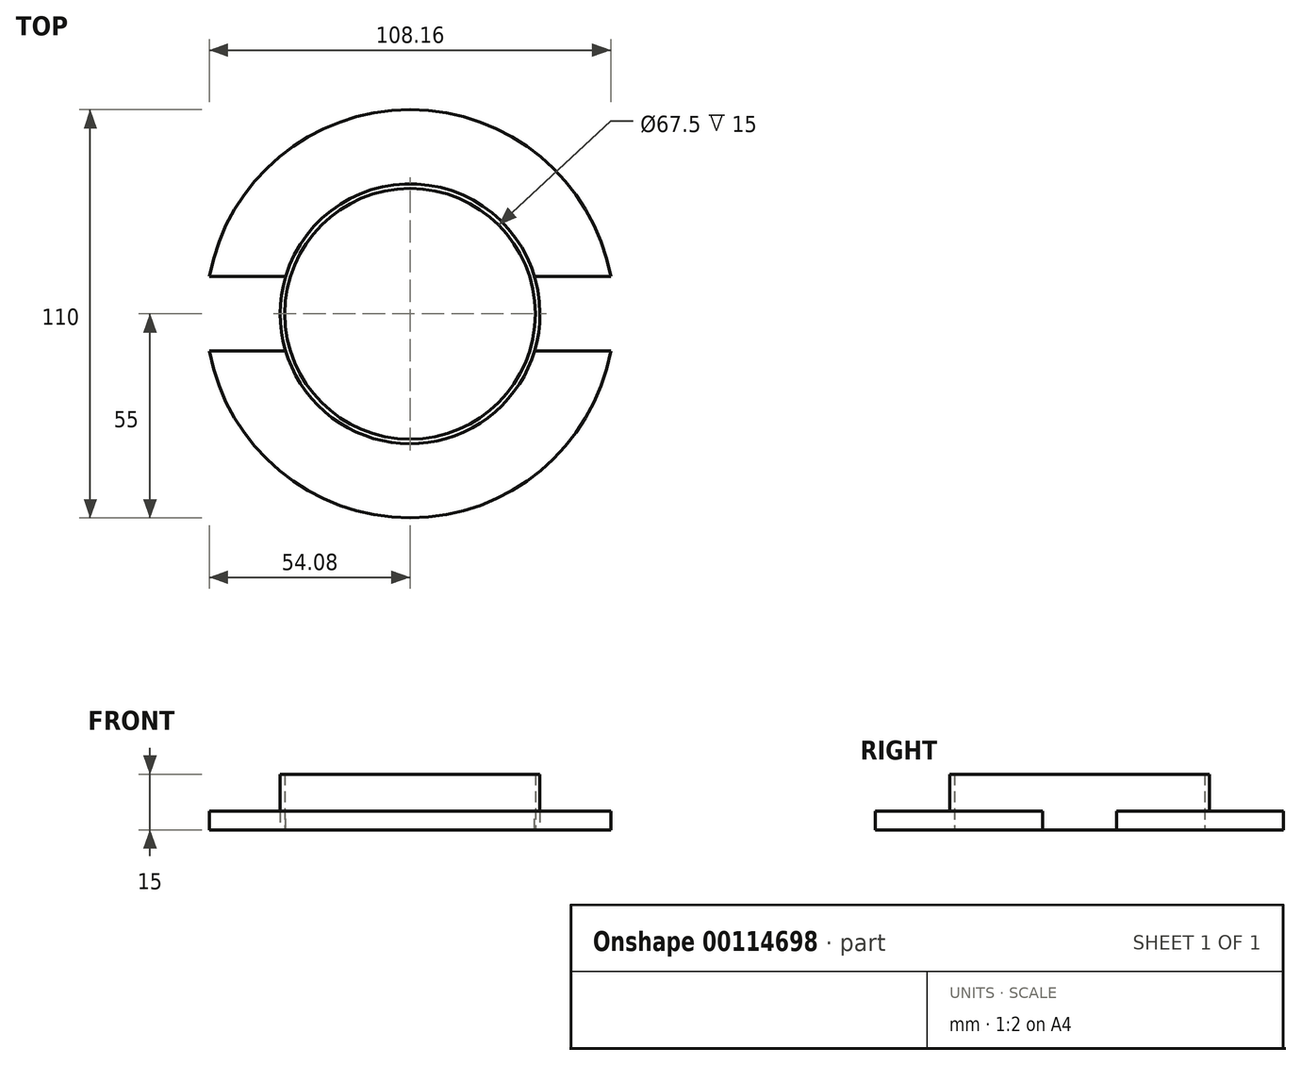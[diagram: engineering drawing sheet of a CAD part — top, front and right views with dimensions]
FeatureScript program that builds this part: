
annotation { "Feature Type Name" : "Feature", "Feature Type Description" : "" }
export const myFeature = defineFeature(function(context is Context, id is Id, definition is map)
    precondition{}
    {
        {
            var Q0;
            Q0=qCreatedBy(makeId("Top.planeOp"),FACE);
            var sketch = newSketch(context, id + "F0", { "sketchPlane" : qUnion([Q0])});
            skCircle(sketch, "E0", {"center": v(0, 0) * mm, "radius": 55 * mm});
            skCircle(sketch, "E1", {"center": v(0, 0) * mm, "radius": 33.75 * mm});
            skSolve(sketch);
        }
        {
            var Q0;
            Q0=makeQuery(id+"F0.imprint","IMPRINT",FACE,{"disambiguationData":[TD([[makeQuery(id+"F0.imprint","IMPRINT",EDGE,{"derivedFrom":sQuery(id+"F0.wireOp",EDGE,"E0")}),1.0]])]});
            extrude(context, id + "F1", {"entities" : qUnion([Q0]), "depth" : 5 * mm});
        }
        {
            var Q0;
            Q0=makeQuery(id+"F1.opExtrude","CAP_FACE",FACE,{"disambiguationData":[OSD([sQuery(id+"F0.wireOp",EDGE,"E0"),sQuery(id+"F0.wireOp",EDGE,"E1")])],"isStart":false});
            var sketch = newSketch(context, id + "F2", { "sketchPlane" : qUnion([Q0])});
            skCircle(sketch, "E2", {"center": v(0, 0) * mm, "radius": 35 * mm});
            skSolve(sketch);
        }
        {
            var Q0;
            Q0=makeQuery(id+"F2.imprint","IMPRINT",FACE,{"disambiguationData":[TD([[makeQuery(id+"F2.imprint","IMPRINT",EDGE,{"derivedFrom":sQuery(id+"F2.wireOp",EDGE,"E2")}),1.0]])]});
            extrude(context, id + "F3", {"entities" : qUnion([Q0]), "operationType" : NewBodyOperationType.ADD, "depth" : 10 * mm});
        }
        {
            var Q0;
            Q0=makeQuery(id+"F1.opExtrude","CAP_FACE",FACE,{"disambiguationData":[OSD([sQuery(id+"F0.wireOp",EDGE,"E0"),sQuery(id+"F0.wireOp",EDGE,"E1")])],"isStart":false});
            var sketch = newSketch(context, id + "F4", { "sketchPlane" : qUnion([Q0])});
            skLineSegment(sketch, "E3", {"start": v(0, 0) * mm, "end": v(0, 10) * mm});
            skLineSegment(sketch, "E4", {"start": v(0, 10) * mm, "end": v(33.54, 10) * mm});
            skLineSegment(sketch, "E5", {"start": v(33.54, 10) * mm, "end": v(61.18, 10) * mm});
            skLineSegment(sketch, "E6", {"start": v(61.18, 10) * mm, "end": v(61.18, -10) * mm});
            skLineSegment(sketch, "E7", {"start": v(61.18, -10) * mm, "end": v(33.54, -10) * mm});
            skLineSegment(sketch, "E8", {"start": v(-33.54, 10) * mm, "end": v(-64.6, 10) * mm});
            skLineSegment(sketch, "E9", {"start": v(-64.6, 10) * mm, "end": v(-64.6, -10) * mm});
            skLineSegment(sketch, "E10", {"start": v(-64.6, -10) * mm, "end": v(-33.54, -10) * mm});
            skCircle(sketch, "E11.0", {"center": v(0, 0) * mm, "radius": 35 * mm});
            skSolve(sketch);
        }
        {
            var Q0;
            {var subQ0=sQuery(id+"F4.wireOp",EDGE,"E11.0");var subQ1=sQuery(id+"F4.wireOp",EDGE,"E8");var subQ2=makeQuery(id+"F4.imprint","INTERSECT",VERTEX,{"derivedFrom":[subQ1,subQ0]});Q0=makeQuery(id+"F4.imprint","IMPRINT",FACE,{"disambiguationData":[TD([[makeQuery(id+"F4.imprint","IMPRINT",EDGE,{"disambiguationData":[TD([[subQ2,-1.0]])],"derivedFrom":subQ1}),1.0]])]});}
            var Q1;
            {var subQ0=sQuery(id+"F4.wireOp",EDGE,"E11.0");var subQ1=sQuery(id+"F4.wireOp",EDGE,"E5");var subQ2=makeQuery(id+"F4.imprint","INTERSECT",VERTEX,{"derivedFrom":[subQ1,subQ0]});Q1=makeQuery(id+"F4.imprint","IMPRINT",FACE,{"disambiguationData":[TD([[makeQuery(id+"F4.imprint","IMPRINT",EDGE,{"disambiguationData":[TD([[subQ2,-1.0]])],"derivedFrom":subQ1}),-1.0]])]});}
            extrude(context, id + "F5", {"entities" : qUnion([Q0, Q1]), "operationType" : NewBodyOperationType.REMOVE, "oppositeDirection" : true, "depth" : 25.4 * mm});
        }
    });
